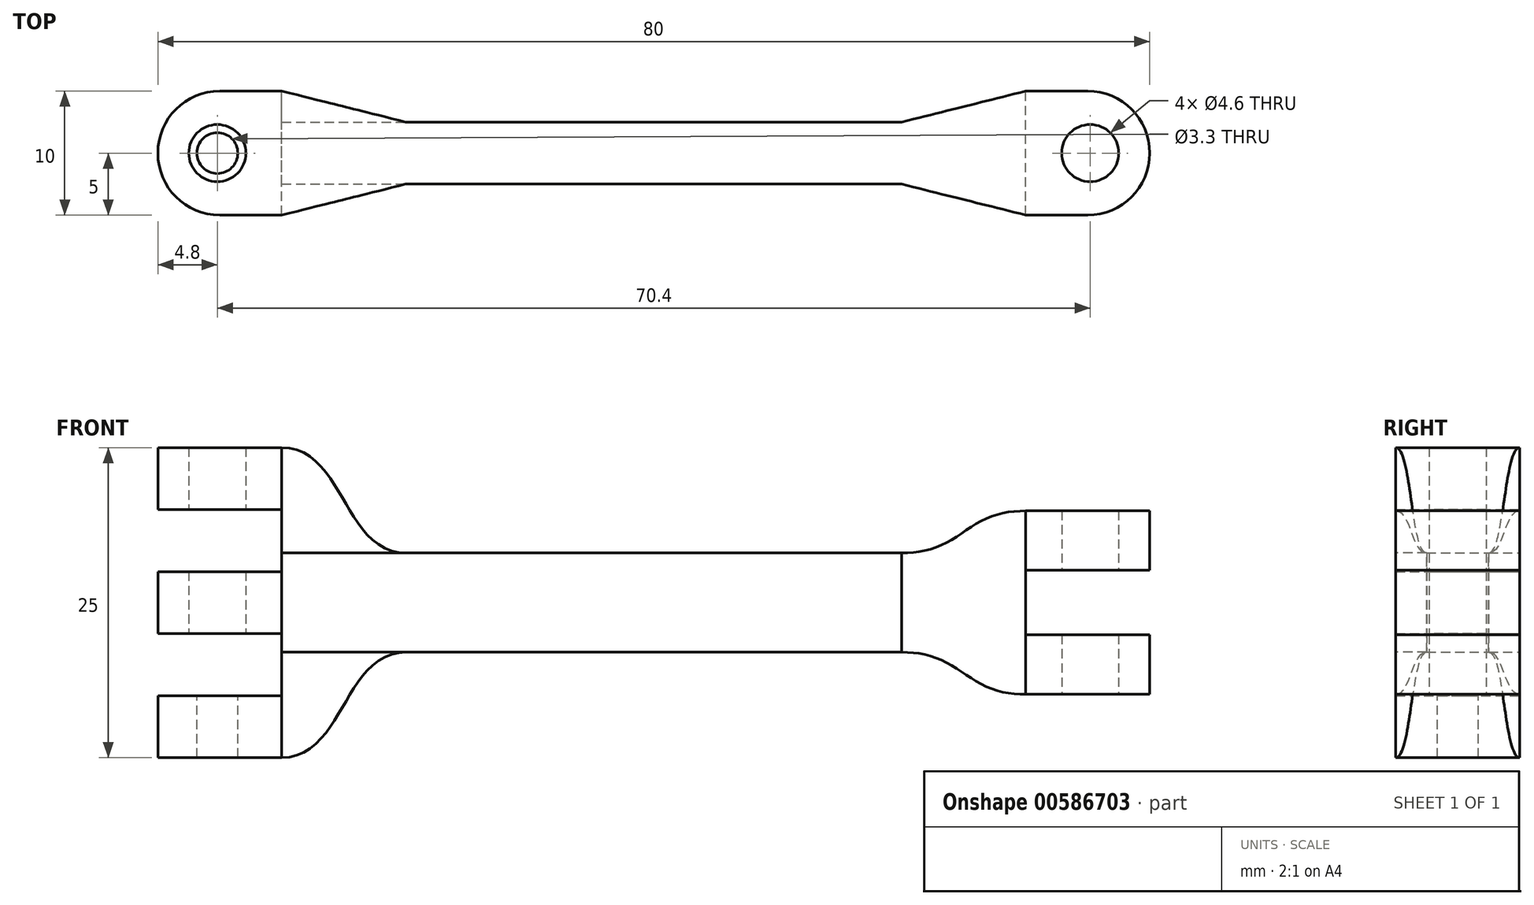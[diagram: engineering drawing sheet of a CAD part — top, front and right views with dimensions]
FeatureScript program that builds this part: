
annotation { "Feature Type Name" : "Feature", "Feature Type Description" : "" }
export const myFeature = defineFeature(function(context is Context, id is Id, definition is map)
    precondition{}
    {
        {
            var Q0;
            Q0=qCreatedBy(makeId("Top.planeOp"),FACE);
            var sketch = newSketch(context, id + "F0", { "sketchPlane" : qUnion([Q0])});
            skLineSegment(sketch, "E0.bottom", {"start": v(-30, 2.5) * mm, "end": v(30, 2.5) * mm});
            skLineSegment(sketch, "E0.top", {"start": v(-30, -2.5) * mm, "end": v(30, -2.5) * mm});
            skLineSegment(sketch, "E0.left", {"start": v(-30, 2.5) * mm, "end": v(-30, -2.5) * mm});
            skLineSegment(sketch, "E0.right", {"start": v(30, 2.5) * mm, "end": v(30, -2.5) * mm});
            skPoint(sketch, "E0.middle", {"position": v(0, 0) * mm});
            skLineSegment(sketch, "E1.bottom", {"start": v(-30, 5) * mm, "end": v(-35, 5) * mm});
            skLineSegment(sketch, "E1.top", {"start": v(-30, -5) * mm, "end": v(-35, -5) * mm});
            skLineSegment(sketch, "E1.left", {"start": v(-30, 5) * mm, "end": v(-30, -5) * mm});
            skLineSegment(sketch, "E1.right", {"start": v(-40, 0) * mm, "end": v(-40, 0) * mm});
            skPoint(sketch, "E1.middle", {"position": v(-35, 0) * mm});
            skPoint(sketch, "E1.middle.positionSnap0", {"position": v(-30, 0) * mm});
            skPoint(sketch, "E1.cornerSnap0", {"position": v(-30, 0) * mm});
            skPoint(sketch, "E1.centerSnap0", {"position": v(-30, 0) * mm});
            skPoint(sketch, "E2.visualSharp", {"position": v(-40, 5) * mm});
            skArc(sketch, "E2.filletArc", {"start": v(-35, 5) * mm, "mid": v(-38.54, 3.54) * mm, "end": v(-40, 0) * mm});
            skPoint(sketch, "E3.visualSharp", {"position": v(-40, -5) * mm});
            skArc(sketch, "E3.filletArc", {"start": v(-40, 0) * mm, "mid": v(-38.54, -3.54) * mm, "end": v(-35, -5) * mm});
            skFitSpline(sketch, "E4", {"points": [v(-30, 5) * mm, v(-20, 2.5) * mm], "startDerivative": vector(11.5, -0.45) * mm, "endDerivative": vector(10.34, 0) * mm});
            skFitSpline(sketch, "E5.MirrorCS", {"points": [v(-30, -5) * mm, v(-20, -2.5) * mm], "startDerivative": vector(11.5, 0.45) * mm, "endDerivative": vector(10.34, 0) * mm});
            skFitSpline(sketch, "E6.MirrorCS", {"points": [v(30, -5) * mm, v(20, -2.5) * mm], "startDerivative": vector(-11.5, 0.45) * mm, "endDerivative": vector(-10.34, 0) * mm});
            skLineSegment(sketch, "E7.MirrorCS", {"start": v(30, 5) * mm, "end": v(35, 5) * mm});
            skLineSegment(sketch, "E8.MirrorCS", {"start": v(30, -5) * mm, "end": v(35, -5) * mm});
            skArc(sketch, "E9.MirrorCS", {"start": v(40, 0) * mm, "mid": v(38.54, -3.54) * mm, "end": v(35, -5) * mm});
            skArc(sketch, "E10.MirrorCS", {"start": v(35, 5) * mm, "mid": v(38.54, 3.54) * mm, "end": v(40, 0) * mm});
            skFitSpline(sketch, "E11.MirrorCS", {"points": [v(30, 5) * mm, v(20, 2.5) * mm], "startDerivative": vector(-11.5, -0.45) * mm, "endDerivative": vector(-10.34, 0) * mm});
            skCircle(sketch, "E12", {"center": v(-34.8, 0) * mm, "radius": 1.65 * mm});
            skCircle(sketch, "E13.MirrorC", {"center": v(34.8, 0) * mm, "radius": 1.65 * mm});
            skCircle(sketch, "E14", {"center": v(-34.8, 0) * mm, "radius": 1.2 * mm});
            skSolve(sketch);
        }
        {
            var Q0;
            {var subQ4=sQuery(id+"F0.wireOp",EDGE,"E0.right");Q0=makeQuery(id+"F0.imprint","IMPRINT",FACE,{"disambiguationData":[TD([[makeQuery(id+"F0.imprint","IMPRINT",EDGE,{"derivedFrom":subQ4}),-1.0]])]});}
            extrude(context, id + "F1", {"entities" : qUnion([Q0]), "endBound" : BoundingType.SYMMETRIC, "depth" : 8 * mm, "offsetDistance" : 25 * mm});
        }
        {
            var Q0;
            Q0=qCreatedBy(makeId("Front.planeOp"),FACE);
            var sketch = newSketch(context, id + "F2", { "sketchPlane" : qUnion([Q0])});
            skLineSegment(sketch, "E15.bottom", {"start": v(-30, 4) * mm, "end": v(30, 4) * mm});
            skLineSegment(sketch, "E15.top", {"start": v(-30, -4) * mm, "end": v(30, -4) * mm});
            skLineSegment(sketch, "E15.left", {"start": v(-30, 4) * mm, "end": v(-30, -4) * mm});
            skLineSegment(sketch, "E15.right", {"start": v(30, 4) * mm, "end": v(30, -4) * mm});
            skPoint(sketch, "E15.middle", {"position": v(0, 0) * mm});
            skLineSegment(sketch, "E16.bottom", {"start": v(-30, 2.5) * mm, "end": v(-40, 2.5) * mm});
            skLineSegment(sketch, "E16.top", {"start": v(-30, -2.5) * mm, "end": v(-40, -2.5) * mm});
            skLineSegment(sketch, "E16.left", {"start": v(-30, 2.5) * mm, "end": v(-30, -2.5) * mm});
            skLineSegment(sketch, "E16.right", {"start": v(-40, 2.5) * mm, "end": v(-40, -2.5) * mm});
            skPoint(sketch, "E16.middle", {"position": v(-35, 0) * mm});
            skLineSegment(sketch, "E17.0.1.0", {"start": v(-30, 12.5) * mm, "end": v(-40, 12.5) * mm});
            skLineSegment(sketch, "E17.0.1.1", {"start": v(-40, 12.5) * mm, "end": v(-40, 7.5) * mm});
            skLineSegment(sketch, "E17.0.1.2", {"start": v(-30, 7.5) * mm, "end": v(-40, 7.5) * mm});
            skPoint(sketch, "E17.0.1.3", {"position": v(-35, 10) * mm});
            skLineSegment(sketch, "E17.direction1", {"start": v(-35, 0) * mm, "end": v(-5, 0) * mm, "construction": true});
            skLineSegment(sketch, "E17.direction2", {"start": v(-35, 0) * mm, "end": v(-35, 10) * mm, "construction": true});
            skLineSegment(sketch, "E18", {"start": v(-30, 7.5) * mm, "end": v(-30, 4) * mm});
            skFitSpline(sketch, "E19", {"points": [v(-30, 12.5) * mm, v(-20, 4) * mm], "startDerivative": vector(15, 0) * mm, "endDerivative": vector(15, 0) * mm});
            skLineSegment(sketch, "E20.MirrorCS", {"start": v(-30, -12.5) * mm, "end": v(-40, -12.5) * mm});
            skLineSegment(sketch, "E21.MirrorCS", {"start": v(-40, -12.5) * mm, "end": v(-40, -7.5) * mm});
            skLineSegment(sketch, "E22.MirrorCS", {"start": v(-30, -7.5) * mm, "end": v(-40, -7.5) * mm});
            skLineSegment(sketch, "E23.MirrorCS", {"start": v(-30, -7.5) * mm, "end": v(-30, -4) * mm});
            skFitSpline(sketch, "E24.MirrorCS", {"points": [v(-30, -12.5) * mm, v(-20, -4) * mm], "startDerivative": vector(15, 0) * mm, "endDerivative": vector(15, 0) * mm});
            skLineSegment(sketch, "E25.bottom", {"start": v(30, 2.6) * mm, "end": v(40, 2.6) * mm});
            skLineSegment(sketch, "E25.top", {"start": v(30, 7.4) * mm, "end": v(40, 7.4) * mm});
            skLineSegment(sketch, "E25.left", {"start": v(30, 2.6) * mm, "end": v(30, 7.4) * mm});
            skLineSegment(sketch, "E25.right", {"start": v(40, 2.6) * mm, "end": v(40, 7.4) * mm});
            skPoint(sketch, "E26", {"position": v(35, 5) * mm});
            skPoint(sketch, "E26.positionSnap0", {"position": v(30, 5) * mm});
            skPoint(sketch, "E26.positionSnap1", {"position": v(35, 7.4) * mm});
            skLineSegment(sketch, "E27.MirrorCS", {"start": v(40, -2.6) * mm, "end": v(40, -7.4) * mm});
            skLineSegment(sketch, "E28.MirrorCS", {"start": v(30, -2.6) * mm, "end": v(40, -2.6) * mm});
            skLineSegment(sketch, "E29.MirrorCS", {"start": v(30, -7.4) * mm, "end": v(40, -7.4) * mm});
            skLineSegment(sketch, "E30.MirrorCS", {"start": v(30, -2.6) * mm, "end": v(30, -7.4) * mm});
            skFitSpline(sketch, "E31", {"points": [v(30, 7.4) * mm, v(20, 4) * mm], "startDerivative": vector(-15, 0) * mm, "endDerivative": vector(-15, 0) * mm});
            skFitSpline(sketch, "E32.MirrorCS", {"points": [v(30, -7.4) * mm, v(20, -4) * mm], "startDerivative": vector(-15, 0) * mm, "endDerivative": vector(-15, 0) * mm});
            skLineSegment(sketch, "E33", {"start": v(-20, 4) * mm, "end": v(-20, -4) * mm});
            skLineSegment(sketch, "E34", {"start": v(20, -4) * mm, "end": v(20, 4) * mm});
            skSolve(sketch);
        }
        {
            var Q0;
            {var subQ3=sQuery(id+"F2.wireOp",EDGE,"E16.left");Q0=makeQuery(id+"F2.imprint","IMPRINT",FACE,{"disambiguationData":[TD([[makeQuery(id+"F2.imprint","IMPRINT",EDGE,{"derivedFrom":subQ3}),1.0]])]});}
            var Q1;
            Q1=makeQuery(id+"F2.imprint","IMPRINT",FACE,{"disambiguationData":[TD([[makeQuery(id+"F2.imprint","IMPRINT",EDGE,{"derivedFrom":sQuery(id+"F2.wireOp",EDGE,"E16.bottom")}),1.0]])]});
            var Q2;
            Q2=makeQuery(id+"F2.imprint","IMPRINT",FACE,{"disambiguationData":[TD([[makeQuery(id+"F2.imprint","IMPRINT",EDGE,{"derivedFrom":sQuery(id+"F2.wireOp",EDGE,"E17.0.1.0")}),1.0]])]});
            var Q3;
            Q3=makeQuery(id+"F2.imprint","IMPRINT",FACE,{"disambiguationData":[TD([[makeQuery(id+"F2.imprint","IMPRINT",EDGE,{"derivedFrom":sQuery(id+"F2.wireOp",EDGE,"E20.MirrorCS")}),-1.0]])]});
            var Q4;
            Q4=makeQuery(id+"F2.imprint","IMPRINT",FACE,{"disambiguationData":[TD([[makeQuery(id+"F2.imprint","IMPRINT",EDGE,{"derivedFrom":sQuery(id+"F2.wireOp",EDGE,"E27.MirrorCS")}),-1.0]])]});
            var Q5;
            {var subQ3=sQuery(id+"F2.wireOp",EDGE,"E32.MirrorCS");Q5=makeQuery(id+"F2.imprint","IMPRINT",FACE,{"disambiguationData":[TD([[makeQuery(id+"F2.imprint","IMPRINT",EDGE,{"derivedFrom":subQ3}),-1.0]])]});}
            var Q6;
            {var subQ3=sQuery(id+"F2.wireOp",EDGE,"E31");Q6=makeQuery(id+"F2.imprint","IMPRINT",FACE,{"disambiguationData":[TD([[makeQuery(id+"F2.imprint","IMPRINT",EDGE,{"derivedFrom":subQ3}),1.0]])]});}
            var Q7;
            {var subQ3=sQuery(id+"F2.wireOp",EDGE,"E25.bottom");Q7=makeQuery(id+"F2.imprint","IMPRINT",FACE,{"disambiguationData":[TD([[makeQuery(id+"F2.imprint","IMPRINT",EDGE,{"derivedFrom":subQ3}),1.0]])]});}
            var Q8;
            {var subQ0=sQuery(id+"F2.wireOp",EDGE,"E15.right");Q8=makeQuery(id+"F2.imprint","IMPRINT",FACE,{"disambiguationData":[TD([[makeQuery(id+"F2.imprint","IMPRINT",EDGE,{"derivedFrom":subQ0}),-1.0]])]});}
            extrude(context, id + "F3", {"entities" : qUnion([Q0, Q1, Q2, Q3, Q4, Q5, Q6, Q7, Q8]), "operationType" : NewBodyOperationType.ADD, "endBound" : BoundingType.SYMMETRIC, "depth" : 10 * mm, "offsetDistance" : 25 * mm});
        }
        {
            var Q0;
            Q0=qCreatedBy(makeId("Top.planeOp"),FACE);
            var sketch = newSketch(context, id + "F4", { "sketchPlane" : qUnion([Q0])});
            skLineSegment(sketch, "E35.bottom", {"start": v(-30, 2.5) * mm, "end": v(30, 2.5) * mm});
            skLineSegment(sketch, "E35.top", {"start": v(-30, -2.5) * mm, "end": v(30, -2.5) * mm});
            skLineSegment(sketch, "E35.left", {"start": v(-30, 2.5) * mm, "end": v(-30, -2.5) * mm});
            skLineSegment(sketch, "E35.right", {"start": v(30, 2.5) * mm, "end": v(30, -2.5) * mm});
            skPoint(sketch, "E35.middle", {"position": v(0, 0) * mm});
            skPoint(sketch, "E36", {"position": v(-30, 0) * mm});
            skLineSegment(sketch, "E37.bottom", {"start": v(-30, 5) * mm, "end": v(-35, 5) * mm});
            skLineSegment(sketch, "E37.top", {"start": v(-30, -5) * mm, "end": v(-35, -5) * mm});
            skLineSegment(sketch, "E37.left", {"start": v(-30, 5) * mm, "end": v(-30, -5) * mm});
            skLineSegment(sketch, "E37.right", {"start": v(-40, 0) * mm, "end": v(-40, 0) * mm});
            skPoint(sketch, "E38.visualSharp", {"position": v(-40, 5) * mm});
            skArc(sketch, "E38.filletArc", {"start": v(-35, 5) * mm, "mid": v(-38.54, 3.54) * mm, "end": v(-40, 0) * mm});
            skPoint(sketch, "E39.visualSharp", {"position": v(-40, -5) * mm});
            skArc(sketch, "E39.filletArc", {"start": v(-40, 0) * mm, "mid": v(-38.54, -3.54) * mm, "end": v(-35, -5) * mm});
            skLineSegment(sketch, "E40", {"start": v(-30, 5) * mm, "end": v(-20, 2.5) * mm});
            skLineSegment(sketch, "E41.MirrorCS", {"start": v(-30, -5) * mm, "end": v(-20, -2.5) * mm});
            skLineSegment(sketch, "E42.MirrorCS", {"start": v(30, -5) * mm, "end": v(20, -2.5) * mm});
            skLineSegment(sketch, "E43.MirrorCS", {"start": v(30, 5) * mm, "end": v(35, 5) * mm});
            skLineSegment(sketch, "E44.MirrorCS", {"start": v(30, -5) * mm, "end": v(35, -5) * mm});
            skArc(sketch, "E45.MirrorCS", {"start": v(40, 0) * mm, "mid": v(38.54, -3.54) * mm, "end": v(35, -5) * mm});
            skArc(sketch, "E46.MirrorCS", {"start": v(35, 5) * mm, "mid": v(38.54, 3.54) * mm, "end": v(40, 0) * mm});
            skLineSegment(sketch, "E47.MirrorCS", {"start": v(30, 5) * mm, "end": v(20, 2.5) * mm});
            skCircle(sketch, "E48", {"center": v(-35.2, 0) * mm, "radius": 2.3 * mm});
            skCircle(sketch, "E49", {"center": v(-35.2, 0) * mm, "radius": 1.65 * mm});
            skCircle(sketch, "E50.MirrorC", {"center": v(35.2, 0) * mm, "radius": 1.65 * mm});
            skCircle(sketch, "E51.MirrorC", {"center": v(35.2, 0) * mm, "radius": 2.3 * mm});
            skSolve(sketch);
        }
        {
            var Q0;
            Q0 = qSketchRegion(id + "F4", true);
            extrude(context, id + "F5", {"entities" : qUnion([Q0]), "operationType" : NewBodyOperationType.INTERSECT, "endBound" : BoundingType.SYMMETRIC, "depth" : 25 * mm, "offsetDistance" : 25 * mm});
        }
        {
            var Q0;
            Q0=makeQuery(id+"F4.imprint","IMPRINT",FACE,{"disambiguationData":[TD([[makeQuery(id+"F4.imprint","IMPRINT",EDGE,{"derivedFrom":sQuery(id+"F4.wireOp",EDGE,"E48")}),1.0]])]});
            var Q1;
            Q1=makeQuery(id+"F3.opExtrude","SWEPT_FACE",FACE,{"disambiguationData":[OSD([sQuery(id+"F2.wireOp",EDGE,"E20.MirrorCS")])]});
            var Q2;
            Q2=makeQuery(id+"F3.opExtrude","SWEPT_FACE",FACE,{"disambiguationData":[OSD([sQuery(id+"F2.wireOp",EDGE,"E22.MirrorCS")])]});
            extrude(context, id + "F6", {"entities" : qUnion([Q0]), "operationType" : NewBodyOperationType.ADD, "endBound" : BoundingType.UP_TO_SURFACE, "oppositeDirection" : true, "depth" : 16.3 * mm, "endBoundEntityFace" : qUnion([Q1]), "offsetDistance" : 25 * mm, "hasSecondDirection" : true, "secondDirectionBound" : SecondDirectionBoundingType.UP_TO_SURFACE, "secondDirectionOppositeDirection" : true, "secondDirectionDepth" : 7.1 * mm, "secondDirectionBoundEntityFace" : qUnion([Q2])});
        }
    });
